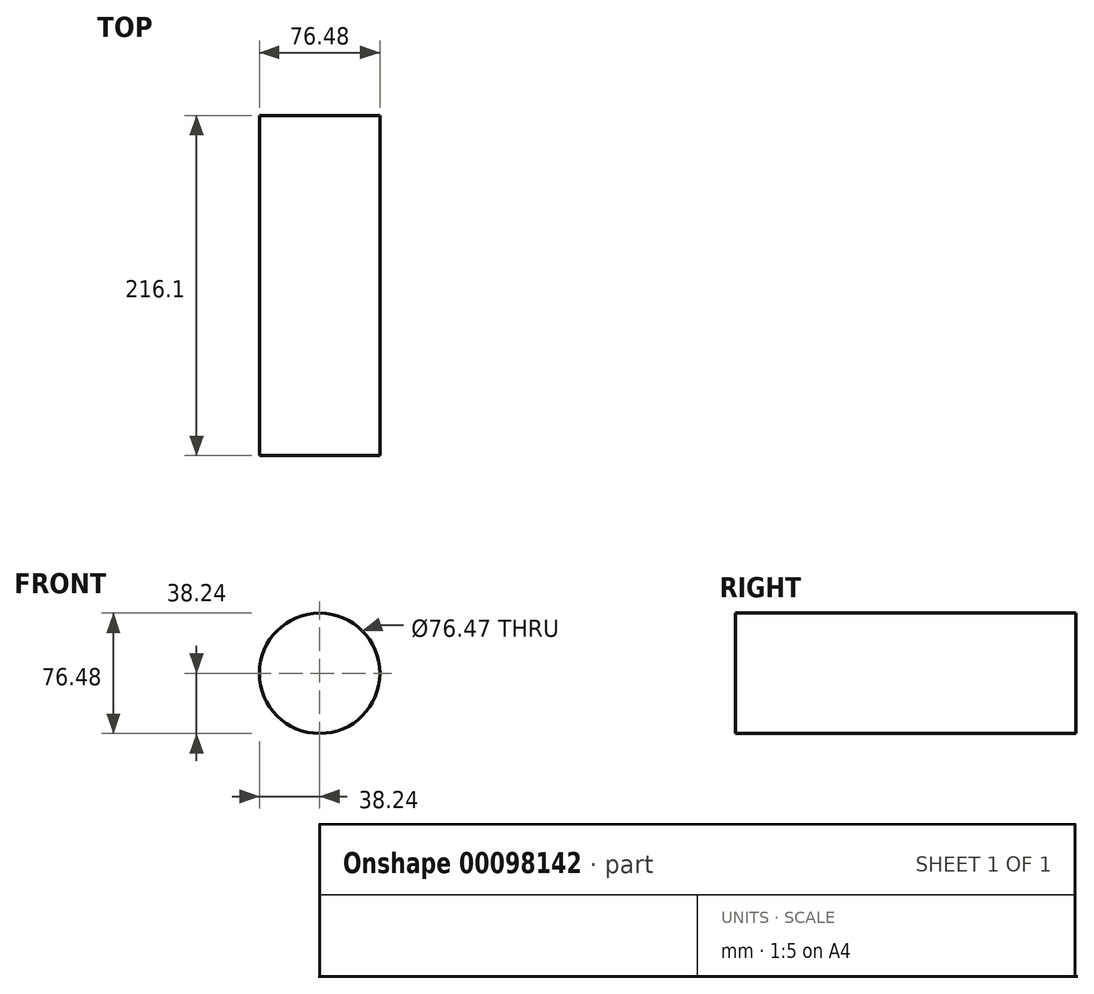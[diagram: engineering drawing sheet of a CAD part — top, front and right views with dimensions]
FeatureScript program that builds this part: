
annotation { "Feature Type Name" : "Feature", "Feature Type Description" : "" }
export const myFeature = defineFeature(function(context is Context, id is Id, definition is map)
    precondition{}
    {
        {
            var Q0;
            Q0=qCreatedBy(makeId("Front.planeOp"),FACE);
            var sketch = newSketch(context, id + "F0", { "sketchPlane" : qUnion([Q0])});
            skCircle(sketch, "E0", {"center": v(0, 0) * mm, "radius": 38.24 * mm});
            skSolve(sketch);
        }
        {
            var Q0;
            Q0=sQuery(id+"F0.wireOp",EDGE,"E0");
            extrude(context, id + "F1", {"bodyType" : ToolBodyType.SURFACE, "surfaceEntities" : qUnion([Q0]), "oppositeDirection" : true, "depth" : 216.1 * mm});
        }
    });
